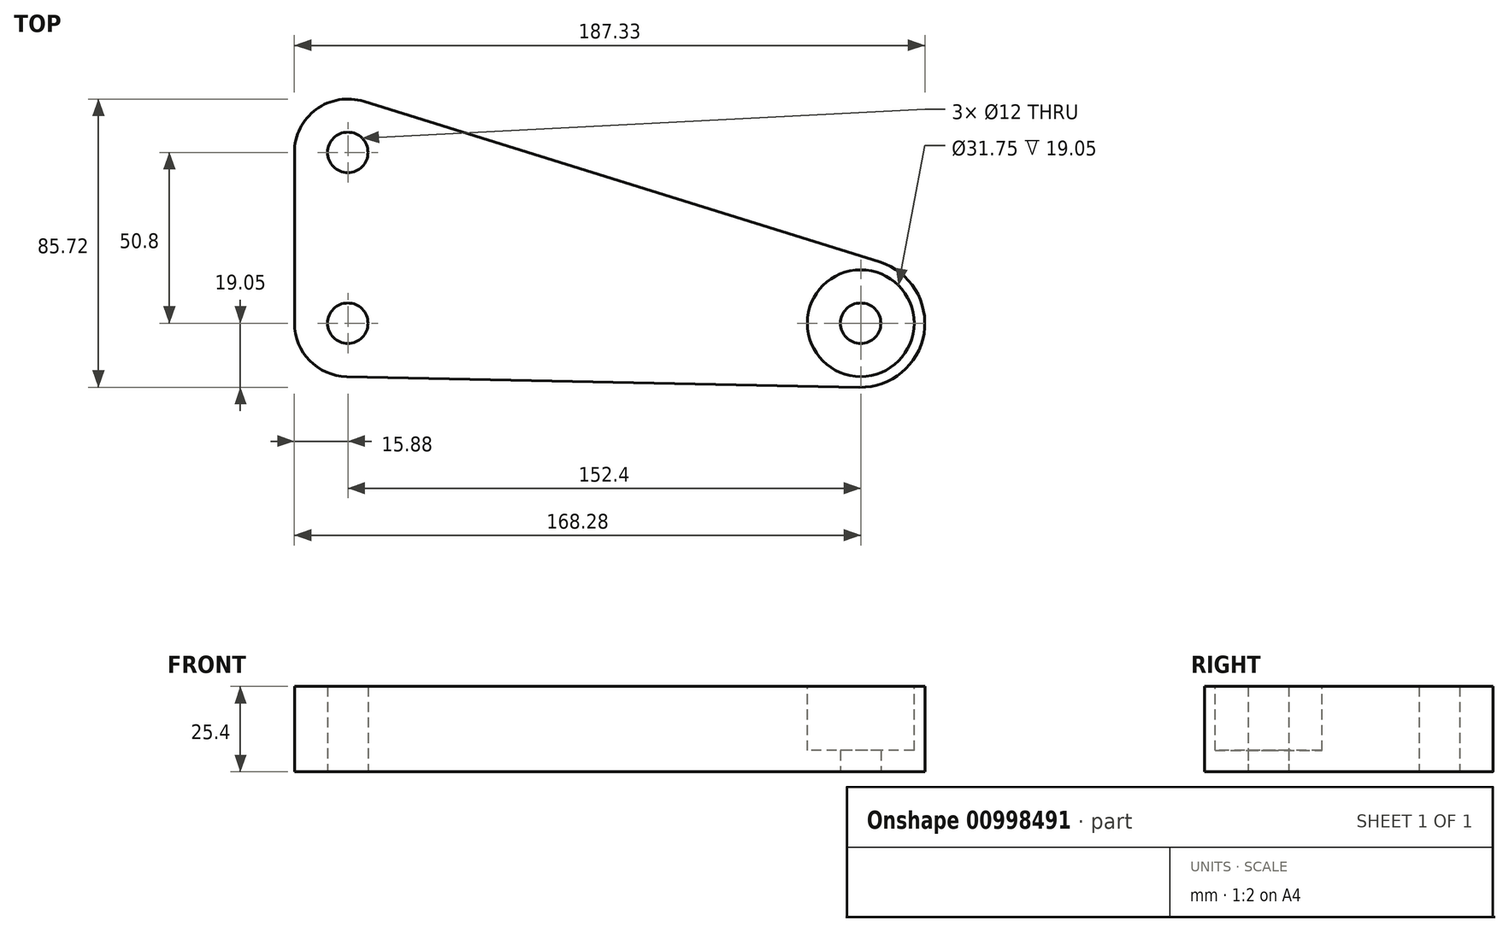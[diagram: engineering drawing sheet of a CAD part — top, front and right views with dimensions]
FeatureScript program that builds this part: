
annotation { "Feature Type Name" : "Feature", "Feature Type Description" : "" }
export const myFeature = defineFeature(function(context is Context, id is Id, definition is map)
    precondition{}
    {
        {
            var Q0;
            Q0=qCreatedBy(makeId("Top.planeOp"),FACE);
            var sketch = newSketch(context, id + "F0", { "sketchPlane" : qUnion([Q0])});
            skLineSegment(sketch, "E0", {"start": v(0, 0) * mm, "end": v(0, -50.8) * mm});
            skLineSegment(sketch, "E1", {"start": v(0, -50.8) * mm, "end": v(152.4, -50.8) * mm});
            skLineSegment(sketch, "E2", {"start": v(152.4, -50.8) * mm, "end": v(0, 0) * mm});
            skSolve(sketch);
        }
        {
            var Q0;
            Q0=qCreatedBy(makeId("Top.planeOp"),FACE);
            var sketch = newSketch(context, id + "F1", { "sketchPlane" : qUnion([Q0])});
            skLineSegment(sketch, "E3.0", {"start": v(-0.33, -66.67) * mm, "end": v(152, -69.85) * mm});
            skLineSegment(sketch, "E3.1", {"start": v(-15.88, 0) * mm, "end": v(-15.88, -50.8) * mm});
            skLineSegment(sketch, "E3.2", {"start": v(158.07, -32.61) * mm, "end": v(4.72, 15.16) * mm});
            skPoint(sketch, "E4.visualSharp", {"position": v(286.6, -72.65) * mm});
            skArc(sketch, "E4.filletArc", {"start": v(152, -69.85) * mm, "mid": v(171.2, -53.86) * mm, "end": v(158.07, -32.61) * mm});
            skPoint(sketch, "E5.visualSharp", {"position": v(-15.88, 21.57) * mm});
            skArc(sketch, "E5.filletArc", {"start": v(4.72, 15.16) * mm, "mid": v(-9.4, 12.79) * mm, "end": v(-15.88, 0) * mm});
            skPoint(sketch, "E6.visualSharp", {"position": v(-15.88, -66.35) * mm});
            skArc(sketch, "E6.filletArc", {"start": v(-15.88, -50.8) * mm, "mid": v(-11.34, -61.9) * mm, "end": v(-0.33, -66.67) * mm});
            skCircle(sketch, "E7", {"center": v(0, 0) * mm, "radius": 6 * mm});
            skCircle(sketch, "E8", {"center": v(0, -50.8) * mm, "radius": 6 * mm});
            skCircle(sketch, "E9", {"center": v(152.4, -50.8) * mm, "radius": 6 * mm});
            skSolve(sketch);
        }
        {
            var Q0;
            Q0 = qSketchRegion(id + "F1", true);
            extrude(context, id + "F2", {"entities" : qUnion([Q0]), "depth" : 25.4 * mm, "offsetDistance" : 25.4 * mm});
        }
        {
            var Q0;
            Q0=makeQuery(id+"F2.opExtrude","CAP_FACE",FACE,{"disambiguationData":[OSD([sQuery(id+"F1.wireOp",EDGE,"E3.0"),sQuery(id+"F1.wireOp",EDGE,"E3.1"),sQuery(id+"F1.wireOp",EDGE,"E3.2"),sQuery(id+"F1.wireOp",EDGE,"E4.filletArc"),sQuery(id+"F1.wireOp",EDGE,"E5.filletArc"),sQuery(id+"F1.wireOp",EDGE,"E6.filletArc"),sQuery(id+"F1.wireOp",EDGE,"E7"),sQuery(id+"F1.wireOp",EDGE,"E8"),sQuery(id+"F1.wireOp",EDGE,"E9")])],"isStart":false});
            var sketch = newSketch(context, id + "F3", { "sketchPlane" : qUnion([Q0])});
            skCircle(sketch, "E10", {"center": v(152.4, -50.8) * mm, "radius": 15.88 * mm});
            skSolve(sketch);
        }
        {
            var Q0;
            Q0 = qSketchRegion(id + "F3", true);
            extrude(context, id + "F4", {"entities" : qUnion([Q0]), "operationType" : NewBodyOperationType.REMOVE, "oppositeDirection" : true, "depth" : 19.05 * mm, "offsetDistance" : 25.4 * mm});
        }
    });
